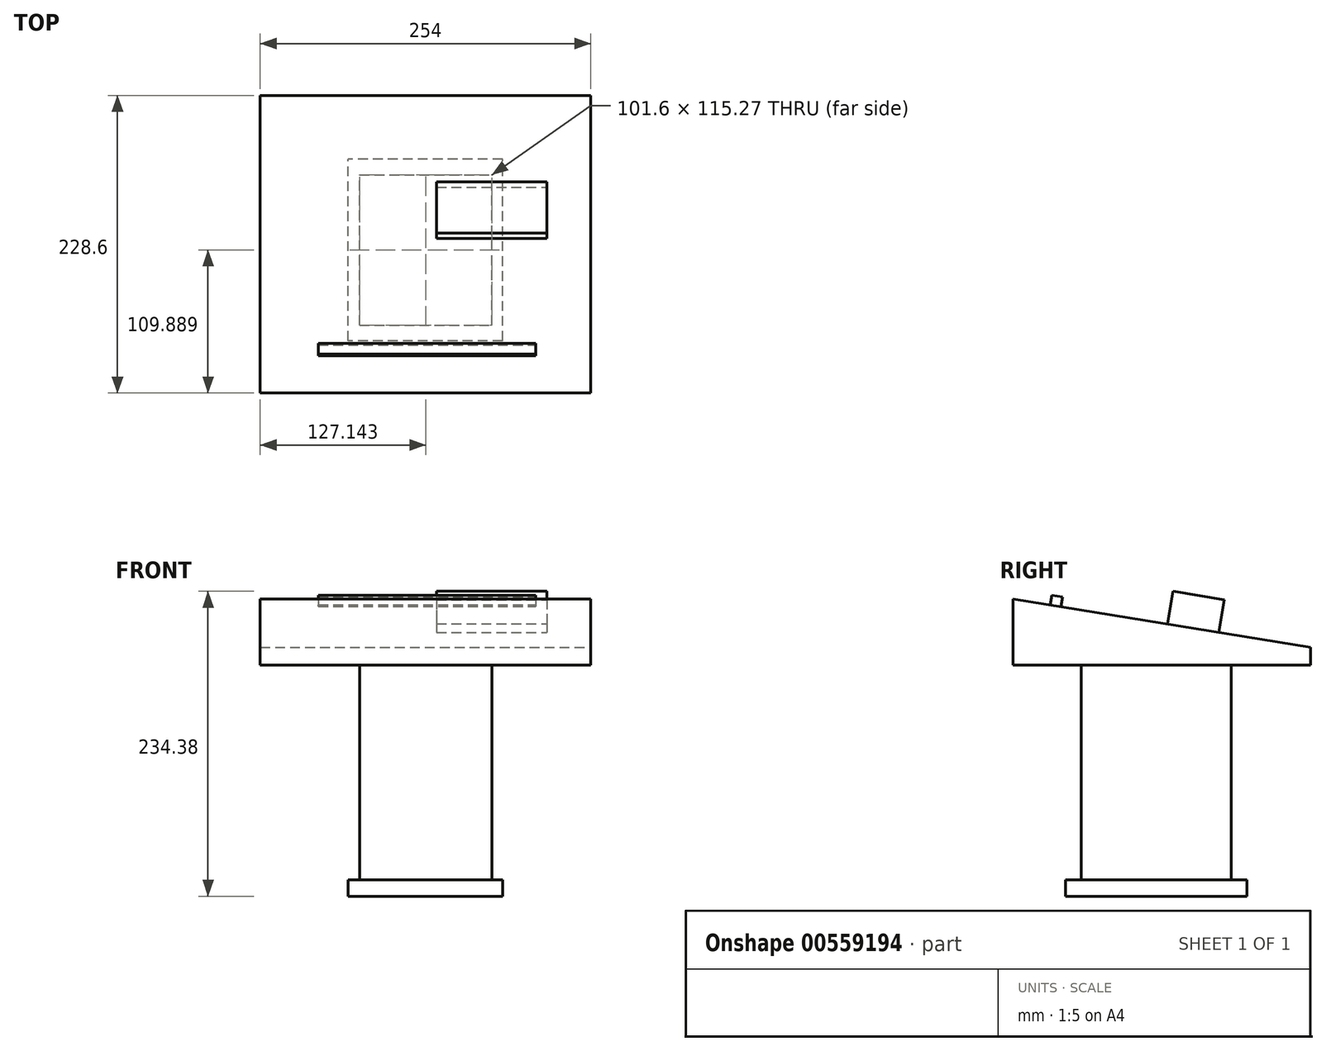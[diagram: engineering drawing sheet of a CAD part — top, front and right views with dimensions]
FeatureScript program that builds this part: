
annotation { "Feature Type Name" : "Feature", "Feature Type Description" : "" }
export const myFeature = defineFeature(function(context is Context, id is Id, definition is map)
    precondition{}
    {
        {
            var Q0;
            Q0=qCreatedBy(makeId("Top.planeOp"),FACE);
            var sketch = newSketch(context, id + "F0", { "sketchPlane" : qUnion([Q0])});
            skLineSegment(sketch, "E0.bottom", {"start": v(-135.48, 115.05) * mm, "end": v(118.52, 115.05) * mm});
            skLineSegment(sketch, "E0.top", {"start": v(-135.48, -113.55) * mm, "end": v(118.52, -113.55) * mm});
            skLineSegment(sketch, "E0.left", {"start": v(-135.48, 115.05) * mm, "end": v(-135.48, -113.55) * mm});
            skLineSegment(sketch, "E0.right", {"start": v(118.52, 115.05) * mm, "end": v(118.52, -113.55) * mm});
            skSolve(sketch);
        }
        {
            var Q0;
            Q0 = qSketchRegion(id + "F0", true);
            extrude(context, id + "F1", {"entities" : qUnion([Q0]), "depth" : 50.8 * mm, "offsetDistance" : 25.4 * mm});
        }
        {
            var Q0;
            Q0=makeQuery(id+"F1.opExtrude","CAP_FACE",FACE,{"disambiguationData":[OSD([sQuery(id+"F0.wireOp",EDGE,"E0.bottom"),sQuery(id+"F0.wireOp",EDGE,"E0.top"),sQuery(id+"F0.wireOp",EDGE,"E0.left"),sQuery(id+"F0.wireOp",EDGE,"E0.right")])],"isStart":true});
            var sketch = newSketch(context, id + "F2", { "sketchPlane" : qUnion([Q0])});
            skLineSegment(sketch, "E1.bottom", {"start": v(-59.14, 61.3) * mm, "end": v(42.46, 61.3) * mm});
            skLineSegment(sketch, "E1.top", {"start": v(-59.14, -53.97) * mm, "end": v(42.46, -53.97) * mm});
            skLineSegment(sketch, "E1.left", {"start": v(-59.14, 61.3) * mm, "end": v(-59.14, -53.97) * mm});
            skLineSegment(sketch, "E1.right", {"start": v(42.46, 61.3) * mm, "end": v(42.46, -53.97) * mm});
            skSolve(sketch);
        }
        {
            var Q0;
            Q0 = qSketchRegion(id + "F2", true);
            extrude(context, id + "F3", {"entities" : qUnion([Q0]), "operationType" : NewBodyOperationType.ADD, "depth" : 165.1 * mm, "offsetDistance" : 25.4 * mm});
        }
        {
            var Q0;
            Q0=makeQuery(id+"F1.opExtrude","SWEPT_FACE",FACE,{"disambiguationData":[OSD([sQuery(id+"F0.wireOp",EDGE,"E0.right")])]});
            var sketch = newSketch(context, id + "F4", { "sketchPlane" : qUnion([Q0])});
            skLineSegment(sketch, "E2", {"start": v(-113.55, 50.8) * mm, "end": v(115.05, 13.64) * mm});
            skSolve(sketch);
        }
        {
            var Q0;
            {var subQ0=sQuery(id+"F4.wireOp",EDGE,"E2");Q0=makeQuery(id+"F4.imprint","IMPRINT",FACE,{"disambiguationData":[TD([[makeQuery(id+"F4.imprint","IMPRINT",EDGE,{"derivedFrom":subQ0}),1.0]])]});}
            extrude(context, id + "F5", {"entities" : qUnion([Q0]), "operationType" : NewBodyOperationType.REMOVE, "oppositeDirection" : true, "depth" : 279.4 * mm, "offsetDistance" : 25.4 * mm});
        }
        {
            var Q0;
            Q0=makeQuery(id+"F3.opExtrude","CAP_FACE",FACE,{"disambiguationData":[OSD([sQuery(id+"F2.wireOp",EDGE,"E1.bottom"),sQuery(id+"F2.wireOp",EDGE,"E1.top"),sQuery(id+"F2.wireOp",EDGE,"E1.left"),sQuery(id+"F2.wireOp",EDGE,"E1.right")])],"isStart":false});
            var sketch = newSketch(context, id + "F6", { "sketchPlane" : qUnion([Q0])});
            skLineSegment(sketch, "E3.bottom", {"start": v(50.63, 73.42) * mm, "end": v(-67.88, 73.42) * mm});
            skLineSegment(sketch, "E3.top", {"start": v(50.63, -66.1) * mm, "end": v(-67.88, -66.1) * mm});
            skLineSegment(sketch, "E3.left", {"start": v(50.63, 73.42) * mm, "end": v(50.63, -66.1) * mm});
            skLineSegment(sketch, "E3.right", {"start": v(-67.88, 73.42) * mm, "end": v(-67.88, -66.1) * mm});
            skSolve(sketch);
        }
        {
            var Q0;
            Q0 = qSketchRegion(id + "F6", true);
            extrude(context, id + "F7", {"entities" : qUnion([Q0]), "operationType" : NewBodyOperationType.ADD, "depth" : 12.7 * mm, "offsetDistance" : 25.4 * mm});
        }
        {
            var Q0;
            Q0=makeQuery(id+"F5.boolean.opBoolean","COPY",FACE,{"derivedFrom":makeQuery(id+"F5.opExtrude","SWEPT_FACE",FACE,{"disambiguationData":[OSD([sQuery(id+"F4.wireOp",EDGE,"E2")])]})});
            var sketch = newSketch(context, id + "F8", { "sketchPlane" : qUnion([Q0])});
            skLineSegment(sketch, "E4.bottom", {"start": v(-90.82, -82.99) * mm, "end": v(76.28, -82.99) * mm});
            skLineSegment(sketch, "E4.top", {"start": v(-90.82, -91.3) * mm, "end": v(76.28, -91.3) * mm});
            skLineSegment(sketch, "E4.left", {"start": v(-90.82, -82.99) * mm, "end": v(-90.82, -91.3) * mm});
            skLineSegment(sketch, "E4.right", {"start": v(76.28, -82.99) * mm, "end": v(76.28, -91.3) * mm});
            skSolve(sketch);
        }
        {
            var Q0;
            Q0 = qSketchRegion(id + "F8", true);
            extrude(context, id + "F9", {"entities" : qUnion([Q0]), "operationType" : NewBodyOperationType.ADD, "depth" : 7.62 * mm, "offsetDistance" : 25.4 * mm});
        }
        {
            var Q0;
            Q0=makeQuery(id+"F5.boolean.opBoolean","COPY",FACE,{"derivedFrom":makeQuery(id+"F5.opExtrude","SWEPT_FACE",FACE,{"disambiguationData":[OSD([sQuery(id+"F4.wireOp",EDGE,"E2")])]})});
            var sketch = newSketch(context, id + "F10", { "sketchPlane" : qUnion([Q0])});
            skLineSegment(sketch, "E5.bottom", {"start": v(0, 0) * mm, "end": v(84.79, 0) * mm});
            skLineSegment(sketch, "E5.top", {"start": v(0, 39.94) * mm, "end": v(84.79, 39.94) * mm});
            skLineSegment(sketch, "E5.left", {"start": v(0, 0) * mm, "end": v(0, 39.94) * mm});
            skLineSegment(sketch, "E5.right", {"start": v(84.79, 0) * mm, "end": v(84.79, 39.94) * mm});
            skSolve(sketch);
        }
        {
            var Q0;
            Q0 = qSketchRegion(id + "F10", true);
            extrude(context, id + "F11", {"entities" : qUnion([Q0]), "operationType" : NewBodyOperationType.ADD, "depth" : 25.4 * mm, "offsetDistance" : 25.4 * mm});
        }
    });
